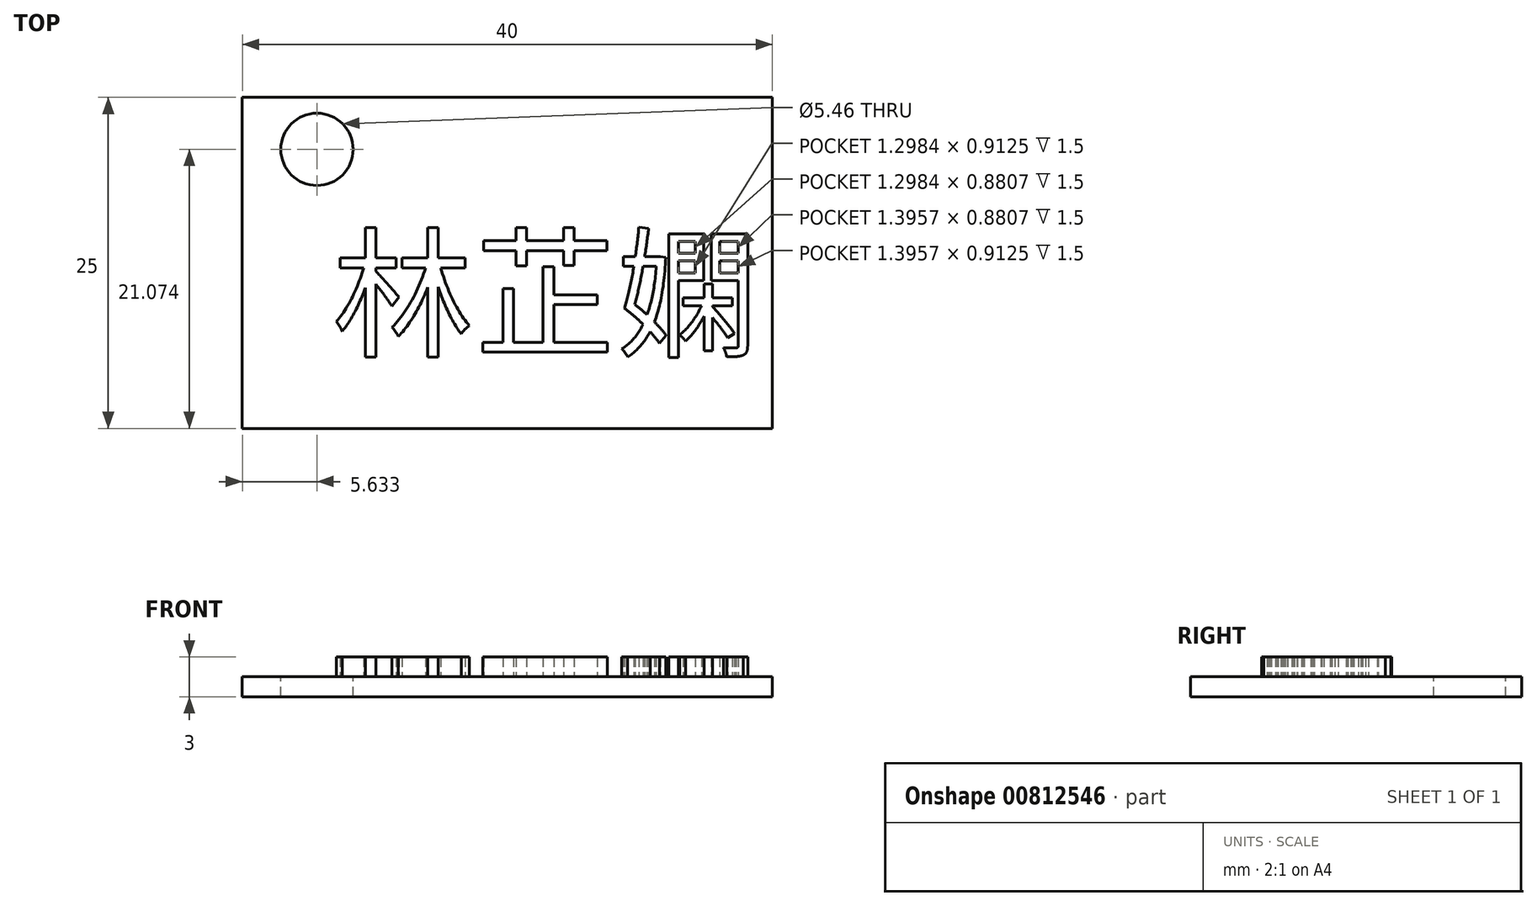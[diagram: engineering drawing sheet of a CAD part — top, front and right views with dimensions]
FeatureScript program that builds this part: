
annotation { "Feature Type Name" : "Feature", "Feature Type Description" : "" }
export const myFeature = defineFeature(function(context is Context, id is Id, definition is map)
    precondition{}
    {
        {
            var Q0;
            Q0=qCreatedBy(makeId("Top.planeOp"),FACE);
            var sketch = newSketch(context, id + "F0", { "sketchPlane" : qUnion([Q0])});
            skLineSegment(sketch, "E0.bottom", {"start": v(-59.07, 50.85) * mm, "end": v(-19.07, 50.85) * mm});
            skLineSegment(sketch, "E0.top", {"start": v(-59.07, 25.85) * mm, "end": v(-19.07, 25.85) * mm});
            skLineSegment(sketch, "E0.left", {"start": v(-59.07, 50.85) * mm, "end": v(-59.07, 25.85) * mm});
            skLineSegment(sketch, "E0.right", {"start": v(-19.07, 50.85) * mm, "end": v(-19.07, 25.85) * mm});
            skSolve(sketch);
        }
        {
            var Q0;
            Q0=makeQuery(id+"F0.imprint","IMPRINT",FACE,{"disambiguationData":[TD([[makeQuery(id+"F0.imprint","IMPRINT",EDGE,{"derivedFrom":sQuery(id+"F0.wireOp",EDGE,"E0.bottom")}),-1.0]])]});
            extrude(context, id + "F1", {"entities" : qUnion([Q0]), "depth" : 1.5 * mm, "offsetDistance" : 25 * mm});
        }
        {
            var Q0;
            Q0=makeQuery(id+"F1.opExtrude","CAP_FACE",FACE,{"disambiguationData":[OSD([sQuery(id+"F0.wireOp",EDGE,"E0.bottom"),sQuery(id+"F0.wireOp",EDGE,"E0.top"),sQuery(id+"F0.wireOp",EDGE,"E0.left"),sQuery(id+"F0.wireOp",EDGE,"E0.right")])],"isStart":false});
            var sketch = newSketch(context, id + "F2", { "sketchPlane" : qUnion([Q0])});
            skText(sketch, "E1", { "text": "林芷嫻", "fontName": "NotoSansCJKsc-Regular.otf"});
            const initialGuessF2  = {"E1": [-0.05232, 0.03204, 1, 0, 0.00773]};
            skSetInitialGuess(sketch, initialGuessF2);
            skSolve(sketch);
        }
        {
            var Q0;
            Q0 = qSketchRegion(id + "F2", true);
            extrude(context, id + "F3", {"entities" : qUnion([Q0]), "operationType" : NewBodyOperationType.ADD, "depth" : 1.5 * mm, "offsetDistance" : 25 * mm});
        }
        {
            var Q0;
            Q0=makeQuery(id+"F2.imprint","IMPRINT",FACE,{"disambiguationData":[TD([[makeQuery(id+"F2.imprint","IMPRINT",EDGE,{"derivedFrom":sQuery(id+"F2.wireOp",EDGE,"E1.sketch_text.stroke-0")}),-1.0]])]});
            var sketch = newSketch(context, id + "F4", { "sketchPlane" : qUnion([Q0])});
            skCircle(sketch, "E2", {"center": v(-53.44, 46.92) * mm, "radius": 2.73 * mm});
            skSolve(sketch);
        }
        {
            var Q0;
            Q0 = qSketchRegion(id + "F4", true);
            extrude(context, id + "F5", {"entities" : qUnion([Q0]), "operationType" : NewBodyOperationType.REMOVE, "oppositeDirection" : true, "depth" : 2 * mm, "offsetDistance" : 25 * mm});
        }
    });
